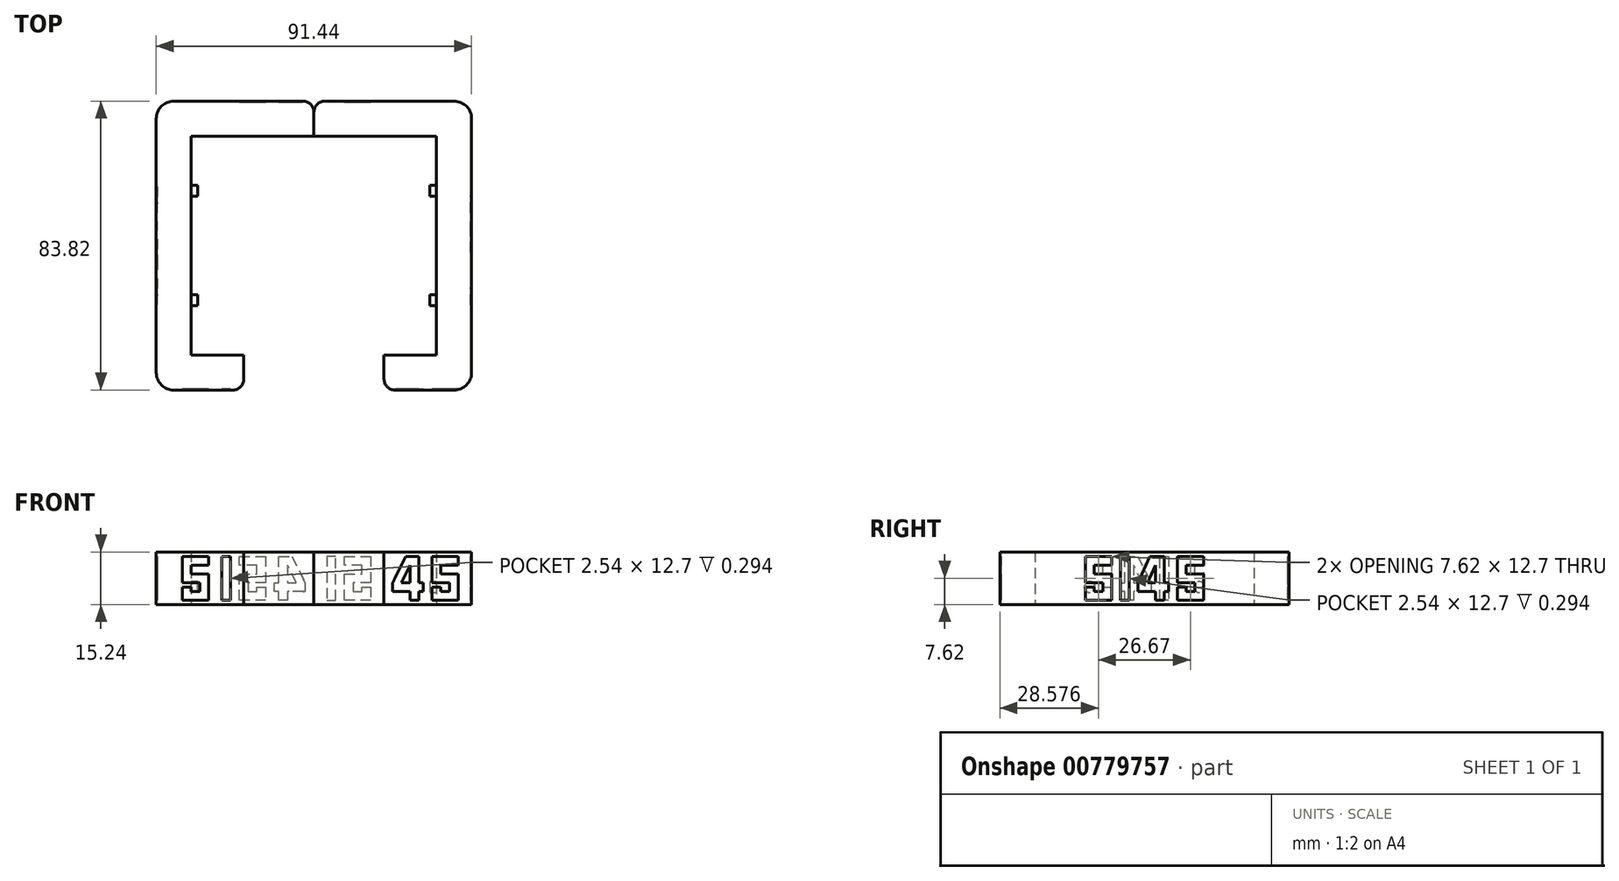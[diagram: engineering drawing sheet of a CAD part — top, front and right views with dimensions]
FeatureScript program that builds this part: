
annotation { "Feature Type Name" : "Feature", "Feature Type Description" : "" }
export const myFeature = defineFeature(function(context is Context, id is Id, definition is map)
    precondition{}
    {
        {
            var Q0;
            Q0=qCreatedBy(makeId("Top.planeOp"),FACE);
            var sketch = newSketch(context, id + "F0", { "sketchPlane" : qUnion([Q0])});
            skLineSegment(sketch, "E0", {"start": v(0, 28.67) * mm, "end": v(0, 38.83) * mm});
            skLineSegment(sketch, "E1", {"start": v(0, 38.83) * mm, "end": v(45.72, 38.83) * mm});
            skLineSegment(sketch, "E2", {"start": v(45.72, 38.83) * mm, "end": v(45.72, -44.99) * mm});
            skLineSegment(sketch, "E3", {"start": v(45.72, -44.99) * mm, "end": v(20.32, -44.99) * mm});
            skLineSegment(sketch, "E4", {"start": v(20.32, -44.99) * mm, "end": v(20.32, -34.83) * mm});
            skLineSegment(sketch, "E5", {"start": v(20.32, -34.83) * mm, "end": v(35.56, -34.83) * mm});
            skLineSegment(sketch, "E6", {"start": v(35.56, -34.83) * mm, "end": v(35.56, 28.67) * mm});
            skLineSegment(sketch, "E7", {"start": v(35.56, 28.67) * mm, "end": v(0, 28.67) * mm});
            skSolve(sketch);
        }
        {
            var Q0;
            Q0=makeQuery(id+"F0.imprint","IMPRINT",FACE,{"disambiguationData":[TD([[makeQuery(id+"F0.imprint","IMPRINT",EDGE,{"derivedFrom":sQuery(id+"F0.wireOp",EDGE,"E0")}),-1.0]])]});
            extrude(context, id + "F1", {"entities" : qUnion([Q0]), "depth" : 15.24 * mm, "offsetDistance" : 25.4 * mm});
        }
        {
            var Q0;
            Q0=makeQuery(id+"F1.opExtrude","SWEPT_FACE",FACE,{"disambiguationData":[OSD([sQuery(id+"F0.wireOp",EDGE,"E6")])]});
            var sketch = newSketch(context, id + "F2", { "sketchPlane" : qUnion([Q0])});
            skCircle(sketch, "E8", {"center": v(-12.8, 5.08) * mm, "radius": 1.59 * mm});
            skPoint(sketch, "E8.centerSnap0", {"position": v(-28.67, 5.08) * mm});
            skCircle(sketch, "E9", {"center": v(18.95, 5.08) * mm, "radius": 1.59 * mm});
            skPoint(sketch, "E9.centerSnap0", {"position": v(34.83, 5.08) * mm});
            skSolve(sketch);
        }
        {
            var Q0;
            Q0=makeQuery(id+"F2.imprint","IMPRINT",FACE,{"disambiguationData":[TD([[makeQuery(id+"F2.imprint","IMPRINT",EDGE,{"derivedFrom":sQuery(id+"F2.wireOp",EDGE,"E8")}),1.0]])]});
            var Q1;
            Q1=makeQuery(id+"F2.imprint","IMPRINT",FACE,{"disambiguationData":[TD([[makeQuery(id+"F2.imprint","IMPRINT",EDGE,{"derivedFrom":sQuery(id+"F2.wireOp",EDGE,"E9")}),1.0]])]});
            extrude(context, id + "F3", {"entities" : qUnion([Q0, Q1]), "operationType" : NewBodyOperationType.ADD, "depth" : 1.9 * mm, "offsetDistance" : 25.4 * mm});
        }
        {
            var Q0;
            Q0=qCreatedBy(makeId("Top.planeOp"),FACE);
            var sketch = newSketch(context, id + "F4", { "sketchPlane" : qUnion([Q0])});
            skLineSegment(sketch, "E10", {"start": v(0, 28.67) * mm, "end": v(-35.56, 28.67) * mm});
            skLineSegment(sketch, "E11", {"start": v(-35.56, 28.67) * mm, "end": v(-35.56, -34.83) * mm});
            skLineSegment(sketch, "E12", {"start": v(-35.56, -34.83) * mm, "end": v(-20.32, -34.83) * mm});
            skLineSegment(sketch, "E13", {"start": v(-20.32, -34.83) * mm, "end": v(-20.32, -44.99) * mm});
            skLineSegment(sketch, "E14", {"start": v(-20.32, -44.99) * mm, "end": v(-45.72, -44.99) * mm});
            skLineSegment(sketch, "E15", {"start": v(-45.72, -44.99) * mm, "end": v(-45.72, 38.83) * mm});
            skLineSegment(sketch, "E16", {"start": v(-45.72, 38.83) * mm, "end": v(0, 38.83) * mm});
            skLineSegment(sketch, "E17", {"start": v(0, 38.83) * mm, "end": v(0, 28.67) * mm});
            skSolve(sketch);
        }
        {
            var Q0;
            Q0=makeQuery(id+"F4.imprint","IMPRINT",FACE,{"disambiguationData":[TD([[makeQuery(id+"F4.imprint","IMPRINT",EDGE,{"derivedFrom":sQuery(id+"F4.wireOp",EDGE,"E10")}),-1.0]])]});
            extrude(context, id + "F5", {"entities" : qUnion([Q0]), "depth" : 15.24 * mm, "offsetDistance" : 25.4 * mm});
        }
        {
            var Q0;
            Q0=makeQuery(id+"F5.opExtrude","SWEPT_FACE",FACE,{"disambiguationData":[OSD([sQuery(id+"F4.wireOp",EDGE,"E11")])]});
            var sketch = newSketch(context, id + "F6", { "sketchPlane" : qUnion([Q0])});
            skCircle(sketch, "E18", {"center": v(-18.95, 5.08) * mm, "radius": 1.59 * mm});
            skPoint(sketch, "E18.centerSnap0", {"position": v(-34.83, 7.62) * mm});
            skCircle(sketch, "E19", {"center": v(12.8, 5.08) * mm, "radius": 1.59 * mm});
            skSolve(sketch);
        }
        {
            var Q0;
            Q0=makeQuery(id+"F6.imprint","IMPRINT",FACE,{"disambiguationData":[TD([[makeQuery(id+"F6.imprint","IMPRINT",EDGE,{"derivedFrom":sQuery(id+"F6.wireOp",EDGE,"E19")}),1.0]])]});
            var Q1;
            Q1=makeQuery(id+"F6.imprint","IMPRINT",FACE,{"disambiguationData":[TD([[makeQuery(id+"F6.imprint","IMPRINT",EDGE,{"derivedFrom":sQuery(id+"F6.wireOp",EDGE,"E18")}),1.0]])]});
            extrude(context, id + "F7", {"entities" : qUnion([Q0, Q1]), "operationType" : NewBodyOperationType.ADD, "depth" : 1.9 * mm, "offsetDistance" : 25.4 * mm});
        }
        {
            var Q0;
            Q0=makeQuery(id+"F1.opExtrude","SWEPT_FACE",FACE,{"disambiguationData":[OSD([sQuery(id+"F0.wireOp",EDGE,"E2")])]});
            var sketch = newSketch(context, id + "F8", { "sketchPlane" : qUnion([Q0])});
            skLineSegment(sketch, "E20", {"start": v(-12.6, 13.97) * mm, "end": v(-20.22, 13.97) * mm});
            skLineSegment(sketch, "E21", {"start": v(-20.22, 13.97) * mm, "end": v(-20.22, 6.35) * mm});
            skLineSegment(sketch, "E22", {"start": v(-20.22, 6.35) * mm, "end": v(-15.14, 6.35) * mm});
            skLineSegment(sketch, "E23", {"start": v(-15.14, 6.35) * mm, "end": v(-15.14, 3.81) * mm});
            skLineSegment(sketch, "E24", {"start": v(-15.14, 3.8) * mm, "end": v(-17.68, 3.8) * mm});
            skLineSegment(sketch, "E25", {"start": v(-17.68, 3.81) * mm, "end": v(-17.68, 5.08) * mm});
            skLineSegment(sketch, "E26", {"start": v(-17.68, 5.08) * mm, "end": v(-20.22, 5.08) * mm});
            skLineSegment(sketch, "E27", {"start": v(-20.22, 5.08) * mm, "end": v(-20.22, 1.27) * mm});
            skLineSegment(sketch, "E28", {"start": v(-20.22, 1.27) * mm, "end": v(-12.6, 1.27) * mm});
            skLineSegment(sketch, "E29", {"start": v(-12.6, 1.27) * mm, "end": v(-12.6, 8.9) * mm});
            skLineSegment(sketch, "E30", {"start": v(-12.6, 8.89) * mm, "end": v(-17.68, 8.89) * mm});
            skLineSegment(sketch, "E31", {"start": v(-17.68, 8.9) * mm, "end": v(-17.68, 11.43) * mm});
            skLineSegment(sketch, "E32", {"start": v(-17.68, 11.43) * mm, "end": v(-12.6, 11.43) * mm});
            skLineSegment(sketch, "E33", {"start": v(-12.6, 11.43) * mm, "end": v(-12.6, 13.97) * mm});
            skLineSegment(sketch, "E34", {"start": v(-10.06, 13.97) * mm, "end": v(-10.06, 1.27) * mm});
            skLineSegment(sketch, "E35", {"start": v(-10.06, 1.27) * mm, "end": v(-7.52, 1.27) * mm});
            skLineSegment(sketch, "E36", {"start": v(-7.52, 1.27) * mm, "end": v(-7.52, 13.97) * mm});
            skLineSegment(sketch, "E37", {"start": v(-7.52, 13.97) * mm, "end": v(-10.06, 13.97) * mm});
            skLineSegment(sketch, "E38", {"start": v(-1.54, 13.97) * mm, "end": v(-4.98, 6.35) * mm});
            skLineSegment(sketch, "E39", {"start": v(-4.98, 6.35) * mm, "end": v(-4.98, 3.81) * mm});
            skLineSegment(sketch, "E40", {"start": v(-4.98, 3.81) * mm, "end": v(0.1, 3.81) * mm});
            skLineSegment(sketch, "E41", {"start": v(0.1, 3.81) * mm, "end": v(0.1, 1.27) * mm});
            skLineSegment(sketch, "E42", {"start": v(0.1, 1.27) * mm, "end": v(2.64, 1.27) * mm});
            skLineSegment(sketch, "E43", {"start": v(2.64, 1.27) * mm, "end": v(2.64, 3.81) * mm});
            skLineSegment(sketch, "E44", {"start": v(2.64, 3.81) * mm, "end": v(3.9, 3.81) * mm});
            skLineSegment(sketch, "E45", {"start": v(3.9, 3.81) * mm, "end": v(3.9, 6.35) * mm});
            skLineSegment(sketch, "E46", {"start": v(3.9, 6.35) * mm, "end": v(2.64, 6.35) * mm});
            skLineSegment(sketch, "E47", {"start": v(2.64, 6.35) * mm, "end": v(2.64, 13.97) * mm});
            skLineSegment(sketch, "E48", {"start": v(2.64, 13.97) * mm, "end": v(-1.54, 13.97) * mm});
            skLineSegment(sketch, "E49", {"start": v(0.1, 6.35) * mm, "end": v(-2.2, 6.35) * mm});
            skLineSegment(sketch, "E50", {"start": v(-2.2, 6.35) * mm, "end": v(0.1, 11.43) * mm});
            skLineSegment(sketch, "E51", {"start": v(0.1, 11.43) * mm, "end": v(0.1, 6.35) * mm});
            skLineSegment(sketch, "E52", {"start": v(14.07, 13.97) * mm, "end": v(6.45, 13.97) * mm});
            skLineSegment(sketch, "E53", {"start": v(6.45, 13.97) * mm, "end": v(6.45, 6.35) * mm});
            skLineSegment(sketch, "E54", {"start": v(6.45, 6.35) * mm, "end": v(11.53, 6.35) * mm});
            skLineSegment(sketch, "E55", {"start": v(11.53, 6.35) * mm, "end": v(11.53, 3.81) * mm});
            skLineSegment(sketch, "E56", {"start": v(11.53, 3.81) * mm, "end": v(8.99, 3.81) * mm});
            skPoint(sketch, "E56.endSnap0", {"position": v(8.99, 6.35) * mm});
            skLineSegment(sketch, "E57", {"start": v(8.99, 3.81) * mm, "end": v(8.99, 5.08) * mm});
            skPoint(sketch, "E57.endSnap0", {"position": v(11.53, 5.08) * mm});
            skLineSegment(sketch, "E58", {"start": v(8.99, 5.08) * mm, "end": v(6.45, 5.08) * mm});
            skLineSegment(sketch, "E59", {"start": v(6.45, 5.08) * mm, "end": v(6.45, 1.27) * mm});
            skLineSegment(sketch, "E60", {"start": v(6.45, 1.27) * mm, "end": v(14.07, 1.27) * mm});
            skLineSegment(sketch, "E61", {"start": v(14.07, 1.27) * mm, "end": v(14.07, 8.9) * mm});
            skLineSegment(sketch, "E62", {"start": v(14.07, 8.9) * mm, "end": v(8.99, 8.9) * mm});
            skLineSegment(sketch, "E63", {"start": v(8.99, 8.9) * mm, "end": v(8.99, 11.43) * mm});
            skLineSegment(sketch, "E64", {"start": v(8.99, 11.43) * mm, "end": v(14.07, 11.43) * mm});
            skLineSegment(sketch, "E65", {"start": v(14.07, 11.43) * mm, "end": v(14.07, 13.97) * mm});
            skLineSegment(sketch, "E66", {"start": v(-20.22, 13.97) * mm, "end": v(-44.99, 13.97) * mm});
            skLineSegment(sketch, "E67", {"start": v(14.07, 13.97) * mm, "end": v(38.83, 13.97) * mm});
            skSolve(sketch);
        }
        {
            var Q0;
            Q0=makeQuery(id+"F8.imprint","IMPRINT",FACE,{"disambiguationData":[TD([[makeQuery(id+"F8.imprint","IMPRINT",EDGE,{"derivedFrom":sQuery(id+"F8.wireOp",EDGE,"E20")}),1.0]])]});
            var Q1;
            Q1=makeQuery(id+"F8.imprint","IMPRINT",FACE,{"disambiguationData":[TD([[makeQuery(id+"F8.imprint","IMPRINT",EDGE,{"derivedFrom":sQuery(id+"F8.wireOp",EDGE,"E34")}),1.0]])]});
            var Q2;
            Q2=makeQuery(id+"F8.imprint","IMPRINT",FACE,{"disambiguationData":[TD([[makeQuery(id+"F8.imprint","IMPRINT",EDGE,{"derivedFrom":sQuery(id+"F8.wireOp",EDGE,"E38")}),1.0]])]});
            var Q3;
            Q3=makeQuery(id+"F8.imprint","IMPRINT",FACE,{"disambiguationData":[TD([[makeQuery(id+"F8.imprint","IMPRINT",EDGE,{"derivedFrom":sQuery(id+"F8.wireOp",EDGE,"E52")}),1.0]])]});
            extrude(context, id + "F9", {"entities" : qUnion([Q0, Q1, Q2, Q3]), "operationType" : NewBodyOperationType.REMOVE, "oppositeDirection" : true, "depth" : 0.8 * mm, "offsetDistance" : 25.4 * mm});
        }
        {
            var Q0;
            Q0=makeQuery(id+"F1.opExtrude","SWEPT_FACE",FACE,{"disambiguationData":[OSD([sQuery(id+"F0.wireOp",EDGE,"E3")])]});
            var sketch = newSketch(context, id + "F10", { "sketchPlane" : qUnion([Q0])});
            skLineSegment(sketch, "E68", {"start": v(22.86, 6.35) * mm, "end": v(22.86, 3.81) * mm});
            skLineSegment(sketch, "E69", {"start": v(22.86, 3.81) * mm, "end": v(27.94, 3.81) * mm});
            skLineSegment(sketch, "E70", {"start": v(27.94, 3.81) * mm, "end": v(27.94, 1.27) * mm});
            skLineSegment(sketch, "E71", {"start": v(27.94, 1.27) * mm, "end": v(30.48, 1.27) * mm});
            skLineSegment(sketch, "E72", {"start": v(30.48, 1.27) * mm, "end": v(30.48, 3.81) * mm});
            skLineSegment(sketch, "E73", {"start": v(30.48, 3.81) * mm, "end": v(31.75, 3.81) * mm});
            skLineSegment(sketch, "E74", {"start": v(31.75, 3.81) * mm, "end": v(31.75, 6.35) * mm});
            skLineSegment(sketch, "E75", {"start": v(31.75, 6.35) * mm, "end": v(30.48, 6.35) * mm});
            skLineSegment(sketch, "E76", {"start": v(30.48, 6.35) * mm, "end": v(30.48, 13.97) * mm});
            skLineSegment(sketch, "E77", {"start": v(30.48, 13.97) * mm, "end": v(26.67, 13.97) * mm});
            skLineSegment(sketch, "E78", {"start": v(26.67, 13.97) * mm, "end": v(22.86, 6.35) * mm});
            skLineSegment(sketch, "E79", {"start": v(27.94, 6.35) * mm, "end": v(25.4, 6.35) * mm});
            skLineSegment(sketch, "E80", {"start": v(25.4, 6.35) * mm, "end": v(27.94, 11.43) * mm});
            skLineSegment(sketch, "E81", {"start": v(27.94, 11.43) * mm, "end": v(27.94, 6.35) * mm});
            skLineSegment(sketch, "E82", {"start": v(41.91, 13.97) * mm, "end": v(34.3, 13.97) * mm});
            skLineSegment(sketch, "E83", {"start": v(34.3, 13.97) * mm, "end": v(34.3, 6.35) * mm});
            skLineSegment(sketch, "E84", {"start": v(34.3, 6.35) * mm, "end": v(39.37, 6.35) * mm});
            skLineSegment(sketch, "E85", {"start": v(39.37, 6.35) * mm, "end": v(39.37, 3.81) * mm});
            skLineSegment(sketch, "E86", {"start": v(39.37, 3.81) * mm, "end": v(36.83, 3.81) * mm});
            skPoint(sketch, "E86.endSnap0", {"position": v(36.83, 6.35) * mm});
            skLineSegment(sketch, "E87", {"start": v(36.83, 3.81) * mm, "end": v(36.83, 5.08) * mm});
            skPoint(sketch, "E87.endSnap0", {"position": v(39.37, 5.08) * mm});
            skLineSegment(sketch, "E88", {"start": v(36.83, 5.08) * mm, "end": v(34.3, 5.08) * mm});
            skLineSegment(sketch, "E89", {"start": v(34.3, 5.08) * mm, "end": v(34.3, 1.27) * mm});
            skLineSegment(sketch, "E90", {"start": v(34.3, 1.27) * mm, "end": v(41.91, 1.27) * mm});
            skLineSegment(sketch, "E91", {"start": v(41.91, 1.27) * mm, "end": v(41.91, 8.89) * mm});
            skLineSegment(sketch, "E92", {"start": v(41.91, 8.89) * mm, "end": v(36.83, 8.89) * mm});
            skLineSegment(sketch, "E93", {"start": v(36.83, 8.89) * mm, "end": v(36.83, 11.43) * mm});
            skLineSegment(sketch, "E94", {"start": v(36.83, 11.43) * mm, "end": v(41.91, 11.43) * mm});
            skLineSegment(sketch, "E95", {"start": v(41.91, 11.43) * mm, "end": v(41.91, 13.97) * mm});
            skSolve(sketch);
        }
        {
            var Q0;
            Q0=makeQuery(id+"F10.imprint","IMPRINT",FACE,{"disambiguationData":[TD([[makeQuery(id+"F10.imprint","IMPRINT",EDGE,{"derivedFrom":sQuery(id+"F10.wireOp",EDGE,"E68")}),1.0]])]});
            var Q1;
            Q1=makeQuery(id+"F10.imprint","IMPRINT",FACE,{"disambiguationData":[TD([[makeQuery(id+"F10.imprint","IMPRINT",EDGE,{"derivedFrom":sQuery(id+"F10.wireOp",EDGE,"E82")}),1.0]])]});
            extrude(context, id + "F11", {"entities" : qUnion([Q0, Q1]), "operationType" : NewBodyOperationType.REMOVE, "oppositeDirection" : true, "depth" : 0.8 * mm, "offsetDistance" : 25.4 * mm});
        }
        {
            var Q0;
            Q0=makeQuery(id+"F5.opExtrude","SWEPT_FACE",FACE,{"disambiguationData":[OSD([sQuery(id+"F4.wireOp",EDGE,"E14")])]});
            var sketch = newSketch(context, id + "F12", { "sketchPlane" : qUnion([Q0])});
            skLineSegment(sketch, "E96", {"start": v(-24.13, 13.97) * mm, "end": v(-26.67, 13.97) * mm});
            skLineSegment(sketch, "E97", {"start": v(-26.67, 13.97) * mm, "end": v(-26.67, 1.27) * mm});
            skLineSegment(sketch, "E98", {"start": v(-26.67, 1.27) * mm, "end": v(-24.13, 1.27) * mm});
            skLineSegment(sketch, "E99", {"start": v(-24.13, 1.27) * mm, "end": v(-24.13, 13.97) * mm});
            skLineSegment(sketch, "E100", {"start": v(-30.48, 13.97) * mm, "end": v(-38.1, 13.97) * mm});
            skLineSegment(sketch, "E101", {"start": v(-38.1, 13.97) * mm, "end": v(-38.1, 6.35) * mm});
            skLineSegment(sketch, "E102", {"start": v(-38.1, 6.35) * mm, "end": v(-33.02, 6.35) * mm});
            skLineSegment(sketch, "E103", {"start": v(-33.02, 6.35) * mm, "end": v(-33.02, 3.8) * mm});
            skLineSegment(sketch, "E104", {"start": v(-33.02, 3.8) * mm, "end": v(-35.56, 3.8) * mm});
            skLineSegment(sketch, "E105", {"start": v(-35.56, 3.8) * mm, "end": v(-35.56, 5.08) * mm});
            skLineSegment(sketch, "E106", {"start": v(-35.56, 5.08) * mm, "end": v(-38.1, 5.08) * mm});
            skLineSegment(sketch, "E107", {"start": v(-38.1, 5.08) * mm, "end": v(-38.1, 1.27) * mm});
            skLineSegment(sketch, "E108", {"start": v(-38.1, 1.27) * mm, "end": v(-30.48, 1.27) * mm});
            skLineSegment(sketch, "E109", {"start": v(-30.48, 1.27) * mm, "end": v(-30.48, 8.9) * mm});
            skLineSegment(sketch, "E110", {"start": v(-30.48, 8.89) * mm, "end": v(-35.56, 8.89) * mm});
            skLineSegment(sketch, "E111", {"start": v(-35.56, 8.89) * mm, "end": v(-35.56, 11.43) * mm});
            skLineSegment(sketch, "E112", {"start": v(-35.56, 11.43) * mm, "end": v(-30.48, 11.43) * mm});
            skLineSegment(sketch, "E113", {"start": v(-30.48, 11.43) * mm, "end": v(-30.48, 13.97) * mm});
            skSolve(sketch);
        }
        {
            var Q0;
            Q0=makeQuery(id+"F12.imprint","IMPRINT",FACE,{"disambiguationData":[TD([[makeQuery(id+"F12.imprint","IMPRINT",EDGE,{"derivedFrom":sQuery(id+"F12.wireOp",EDGE,"E100")}),1.0]])]});
            var Q1;
            Q1=makeQuery(id+"F12.imprint","IMPRINT",FACE,{"disambiguationData":[TD([[makeQuery(id+"F12.imprint","IMPRINT",EDGE,{"derivedFrom":sQuery(id+"F12.wireOp",EDGE,"E96")}),1.0]])]});
            extrude(context, id + "F13", {"entities" : qUnion([Q0, Q1]), "operationType" : NewBodyOperationType.REMOVE, "oppositeDirection" : true, "depth" : 0.8 * mm, "offsetDistance" : 25.4 * mm});
        }
        {
            var Q0;
            Q0=makeQuery(id+"F5.opExtrude","SWEPT_FACE",FACE,{"disambiguationData":[OSD([sQuery(id+"F4.wireOp",EDGE,"E15")])]});
            var sketch = newSketch(context, id + "F14", { "sketchPlane" : qUnion([Q0])});
            skLineSegment(sketch, "E114", {"start": v(-6.45, 13.97) * mm, "end": v(-14.07, 13.97) * mm});
            skLineSegment(sketch, "E115", {"start": v(-14.07, 13.97) * mm, "end": v(-14.07, 6.35) * mm});
            skLineSegment(sketch, "E116", {"start": v(-14.07, 6.35) * mm, "end": v(-8.99, 6.35) * mm});
            skLineSegment(sketch, "E117", {"start": v(-8.99, 6.35) * mm, "end": v(-8.99, 3.8) * mm});
            skLineSegment(sketch, "E118", {"start": v(-8.99, 3.81) * mm, "end": v(-11.53, 3.81) * mm});
            skLineSegment(sketch, "E119", {"start": v(-11.53, 3.8) * mm, "end": v(-11.53, 5.08) * mm});
            skLineSegment(sketch, "E120", {"start": v(-11.53, 5.08) * mm, "end": v(-14.07, 5.08) * mm});
            skLineSegment(sketch, "E121", {"start": v(-14.07, 5.08) * mm, "end": v(-14.07, 1.27) * mm});
            skLineSegment(sketch, "E122", {"start": v(-14.07, 1.27) * mm, "end": v(-6.45, 1.27) * mm});
            skLineSegment(sketch, "E123", {"start": v(-6.45, 1.27) * mm, "end": v(-6.45, 8.9) * mm});
            skLineSegment(sketch, "E124", {"start": v(-6.45, 8.9) * mm, "end": v(-11.53, 8.9) * mm});
            skLineSegment(sketch, "E125", {"start": v(-11.53, 8.89) * mm, "end": v(-11.53, 11.43) * mm});
            skLineSegment(sketch, "E126", {"start": v(-11.53, 11.43) * mm, "end": v(-6.45, 11.43) * mm});
            skLineSegment(sketch, "E127", {"start": v(-6.45, 11.43) * mm, "end": v(-6.45, 13.97) * mm});
            skLineSegment(sketch, "E128", {"start": v(-3.9, 13.97) * mm, "end": v(-3.9, 1.27) * mm});
            skLineSegment(sketch, "E129", {"start": v(-3.9, 1.27) * mm, "end": v(-1.37, 1.27) * mm});
            skLineSegment(sketch, "E130", {"start": v(-1.37, 1.27) * mm, "end": v(-1.37, 13.97) * mm});
            skLineSegment(sketch, "E131", {"start": v(-1.37, 13.97) * mm, "end": v(-3.9, 13.97) * mm});
            skLineSegment(sketch, "E132", {"start": v(4.98, 13.97) * mm, "end": v(1.17, 6.35) * mm});
            skLineSegment(sketch, "E133", {"start": v(1.17, 6.35) * mm, "end": v(1.17, 3.81) * mm});
            skLineSegment(sketch, "E134", {"start": v(1.17, 3.81) * mm, "end": v(6.25, 3.81) * mm});
            skLineSegment(sketch, "E135", {"start": v(6.25, 3.81) * mm, "end": v(6.25, 1.27) * mm});
            skLineSegment(sketch, "E136", {"start": v(6.25, 1.27) * mm, "end": v(8.8, 1.27) * mm});
            skLineSegment(sketch, "E137", {"start": v(8.8, 1.27) * mm, "end": v(8.8, 3.81) * mm});
            skLineSegment(sketch, "E138", {"start": v(8.8, 3.81) * mm, "end": v(10.06, 3.81) * mm});
            skLineSegment(sketch, "E139", {"start": v(10.06, 3.81) * mm, "end": v(10.06, 6.35) * mm});
            skLineSegment(sketch, "E140", {"start": v(10.06, 6.35) * mm, "end": v(8.8, 6.35) * mm});
            skLineSegment(sketch, "E141", {"start": v(8.8, 6.35) * mm, "end": v(8.8, 13.97) * mm});
            skLineSegment(sketch, "E142", {"start": v(8.8, 13.97) * mm, "end": v(4.98, 13.97) * mm});
            skLineSegment(sketch, "E143", {"start": v(6.25, 6.35) * mm, "end": v(3.71, 6.35) * mm});
            skLineSegment(sketch, "E144", {"start": v(3.71, 6.35) * mm, "end": v(6.25, 11.43) * mm});
            skLineSegment(sketch, "E145", {"start": v(6.25, 11.43) * mm, "end": v(6.25, 6.35) * mm});
            skLineSegment(sketch, "E146", {"start": v(20.22, 13.97) * mm, "end": v(12.6, 13.97) * mm});
            skLineSegment(sketch, "E147", {"start": v(12.6, 13.97) * mm, "end": v(12.6, 6.35) * mm});
            skLineSegment(sketch, "E148", {"start": v(12.6, 6.35) * mm, "end": v(17.68, 6.35) * mm});
            skLineSegment(sketch, "E149", {"start": v(17.68, 6.35) * mm, "end": v(17.68, 3.81) * mm});
            skLineSegment(sketch, "E150", {"start": v(17.68, 3.81) * mm, "end": v(15.14, 3.81) * mm});
            skLineSegment(sketch, "E151", {"start": v(15.14, 3.81) * mm, "end": v(15.14, 5.08) * mm});
            skLineSegment(sketch, "E152", {"start": v(15.14, 5.08) * mm, "end": v(12.6, 5.08) * mm});
            skLineSegment(sketch, "E153", {"start": v(12.6, 5.08) * mm, "end": v(12.6, 1.27) * mm});
            skLineSegment(sketch, "E154", {"start": v(12.6, 1.27) * mm, "end": v(20.22, 1.27) * mm});
            skLineSegment(sketch, "E155", {"start": v(20.22, 1.27) * mm, "end": v(20.22, 8.9) * mm});
            skLineSegment(sketch, "E156", {"start": v(20.22, 8.9) * mm, "end": v(15.14, 8.9) * mm});
            skLineSegment(sketch, "E157", {"start": v(15.14, 8.9) * mm, "end": v(15.14, 11.43) * mm});
            skLineSegment(sketch, "E158", {"start": v(15.14, 11.43) * mm, "end": v(20.22, 11.43) * mm});
            skLineSegment(sketch, "E159", {"start": v(20.22, 11.43) * mm, "end": v(20.22, 13.97) * mm});
            skLineSegment(sketch, "E160", {"start": v(-38.83, 13.97) * mm, "end": v(-14.07, 13.97) * mm});
            skLineSegment(sketch, "E161", {"start": v(44.99, 13.97) * mm, "end": v(20.22, 13.97) * mm});
            skSolve(sketch);
        }
        {
            var Q0;
            Q0 = qSketchRegion(id + "F14", true);
            extrude(context, id + "F15", {"entities" : qUnion([Q0]), "operationType" : NewBodyOperationType.REMOVE, "oppositeDirection" : true, "depth" : 0.8 * mm, "offsetDistance" : 25.4 * mm});
        }
        {
            var Q0;
            Q0=makeQuery(id+"F1.opExtrude","SWEPT_FACE",FACE,{"disambiguationData":[OSD([sQuery(id+"F0.wireOp",EDGE,"E1")])]});
            var sketch = newSketch(context, id + "F16", { "sketchPlane" : qUnion([Q0])});
            skLineSegment(sketch, "E162", {"start": v(-8.9, 13.97) * mm, "end": v(-16.51, 13.97) * mm});
            skLineSegment(sketch, "E163", {"start": v(-16.51, 13.97) * mm, "end": v(-16.51, 6.35) * mm});
            skLineSegment(sketch, "E164", {"start": v(-16.51, 6.35) * mm, "end": v(-11.43, 6.35) * mm});
            skLineSegment(sketch, "E165", {"start": v(-11.43, 6.35) * mm, "end": v(-11.43, 3.81) * mm});
            skLineSegment(sketch, "E166", {"start": v(-11.43, 3.81) * mm, "end": v(-13.97, 3.8) * mm});
            skLineSegment(sketch, "E167", {"start": v(-13.97, 3.8) * mm, "end": v(-13.97, 5.08) * mm});
            skLineSegment(sketch, "E168", {"start": v(-13.97, 5.08) * mm, "end": v(-16.51, 5.08) * mm});
            skLineSegment(sketch, "E169", {"start": v(-16.51, 5.08) * mm, "end": v(-16.51, 1.27) * mm});
            skLineSegment(sketch, "E170", {"start": v(-16.51, 1.27) * mm, "end": v(-8.9, 1.27) * mm});
            skLineSegment(sketch, "E171", {"start": v(-8.9, 1.27) * mm, "end": v(-8.9, 8.89) * mm});
            skLineSegment(sketch, "E172", {"start": v(-8.9, 8.9) * mm, "end": v(-13.97, 8.89) * mm});
            skLineSegment(sketch, "E173", {"start": v(-13.97, 8.89) * mm, "end": v(-13.97, 11.43) * mm});
            skLineSegment(sketch, "E174", {"start": v(-13.97, 11.43) * mm, "end": v(-8.9, 11.43) * mm});
            skLineSegment(sketch, "E175", {"start": v(-8.9, 11.43) * mm, "end": v(-8.9, 13.97) * mm});
            skLineSegment(sketch, "E176", {"start": v(-6.35, 13.97) * mm, "end": v(-3.81, 13.97) * mm});
            skLineSegment(sketch, "E177", {"start": v(-3.81, 13.97) * mm, "end": v(-3.81, 1.27) * mm});
            skLineSegment(sketch, "E178", {"start": v(-3.81, 1.27) * mm, "end": v(-6.35, 1.27) * mm});
            skLineSegment(sketch, "E179", {"start": v(-6.35, 1.27) * mm, "end": v(-6.35, 13.97) * mm});
            skSolve(sketch);
        }
        {
            var Q0;
            Q0 = qSketchRegion(id + "F16", true);
            extrude(context, id + "F17", {"entities" : qUnion([Q0]), "operationType" : NewBodyOperationType.REMOVE, "oppositeDirection" : true, "depth" : 0.8 * mm, "offsetDistance" : 25.4 * mm});
        }
        {
            var Q0;
            Q0=makeQuery(id+"F5.opExtrude","SWEPT_FACE",FACE,{"disambiguationData":[OSD([sQuery(id+"F4.wireOp",EDGE,"E16")])]});
            var sketch = newSketch(context, id + "F18", { "sketchPlane" : qUnion([Q0])});
            skLineSegment(sketch, "E180", {"start": v(2.54, 6.35) * mm, "end": v(2.54, 3.81) * mm});
            skLineSegment(sketch, "E181", {"start": v(2.54, 3.81) * mm, "end": v(7.62, 3.81) * mm});
            skLineSegment(sketch, "E182", {"start": v(7.62, 3.81) * mm, "end": v(7.62, 1.27) * mm});
            skLineSegment(sketch, "E183", {"start": v(7.62, 1.27) * mm, "end": v(10.16, 1.27) * mm});
            skLineSegment(sketch, "E184", {"start": v(10.16, 1.27) * mm, "end": v(10.16, 3.81) * mm});
            skLineSegment(sketch, "E185", {"start": v(10.16, 3.81) * mm, "end": v(11.43, 3.81) * mm});
            skLineSegment(sketch, "E186", {"start": v(11.43, 3.81) * mm, "end": v(11.43, 6.35) * mm});
            skLineSegment(sketch, "E187", {"start": v(11.43, 6.35) * mm, "end": v(10.16, 6.35) * mm});
            skLineSegment(sketch, "E188", {"start": v(10.16, 6.35) * mm, "end": v(10.16, 13.97) * mm});
            skLineSegment(sketch, "E189", {"start": v(10.16, 13.97) * mm, "end": v(6.35, 13.97) * mm});
            skLineSegment(sketch, "E190", {"start": v(6.35, 13.97) * mm, "end": v(2.54, 6.35) * mm});
            skLineSegment(sketch, "E191", {"start": v(7.62, 6.35) * mm, "end": v(5.08, 6.35) * mm});
            skLineSegment(sketch, "E192", {"start": v(5.08, 6.35) * mm, "end": v(7.62, 11.43) * mm});
            skLineSegment(sketch, "E193", {"start": v(7.62, 11.43) * mm, "end": v(7.62, 6.35) * mm});
            skLineSegment(sketch, "E194", {"start": v(21.6, 13.97) * mm, "end": v(13.97, 13.97) * mm});
            skLineSegment(sketch, "E195", {"start": v(13.97, 13.97) * mm, "end": v(13.97, 6.35) * mm});
            skLineSegment(sketch, "E196", {"start": v(13.97, 6.35) * mm, "end": v(19.05, 6.35) * mm});
            skLineSegment(sketch, "E197", {"start": v(19.05, 6.35) * mm, "end": v(19.05, 3.81) * mm});
            skLineSegment(sketch, "E198", {"start": v(19.05, 3.81) * mm, "end": v(16.51, 3.81) * mm});
            skLineSegment(sketch, "E199", {"start": v(16.51, 3.81) * mm, "end": v(16.51, 5.08) * mm});
            skLineSegment(sketch, "E200", {"start": v(16.51, 5.08) * mm, "end": v(13.97, 5.08) * mm});
            skLineSegment(sketch, "E201", {"start": v(13.97, 5.08) * mm, "end": v(13.97, 1.27) * mm});
            skLineSegment(sketch, "E202", {"start": v(13.97, 1.27) * mm, "end": v(21.59, 1.27) * mm});
            skLineSegment(sketch, "E203", {"start": v(21.59, 1.27) * mm, "end": v(21.59, 8.9) * mm});
            skLineSegment(sketch, "E204", {"start": v(21.59, 8.9) * mm, "end": v(16.51, 8.9) * mm});
            skLineSegment(sketch, "E205", {"start": v(16.51, 8.9) * mm, "end": v(16.51, 11.43) * mm});
            skLineSegment(sketch, "E206", {"start": v(16.51, 11.43) * mm, "end": v(21.59, 11.43) * mm});
            skLineSegment(sketch, "E207", {"start": v(21.59, 11.43) * mm, "end": v(21.59, 13.97) * mm});
            skSolve(sketch);
        }
        {
            var Q0;
            Q0 = qSketchRegion(id + "F18", true);
            extrude(context, id + "F19", {"entities" : qUnion([Q0]), "operationType" : NewBodyOperationType.REMOVE, "oppositeDirection" : true, "depth" : 0.8 * mm, "offsetDistance" : 25.4 * mm});
        }
        {
            var Q0;
            Q0=makeQuery(id+"F5.opExtrude","SWEPT_EDGE",EDGE,{"disambiguationData":[OSD([sQuery(id+"F4.wireOp",EDGE,"E15"),sQuery(id+"F4.wireOp",EDGE,"E16")])]});
            var Q1;
            Q1=makeQuery(id+"F5.opExtrude","SWEPT_EDGE",EDGE,{"disambiguationData":[OSD([sQuery(id+"F4.wireOp",EDGE,"E14"),sQuery(id+"F4.wireOp",EDGE,"E15")])]});
            fillet(context, id + "F20", {"entities" : qUnion([Q0, Q1]), "tangentPropagation" : true, "radius" : 5.08 * mm, "defaultsChanged" : true, "vertexSettings" : [], "allowEdgeOverflow" : false});
        }
        {
            var Q0;
            Q0=makeQuery(id+"F1.opExtrude","SWEPT_EDGE",EDGE,{"disambiguationData":[OSD([sQuery(id+"F0.wireOp",EDGE,"E2"),sQuery(id+"F0.wireOp",EDGE,"E3")])]});
            var Q1;
            Q1=makeQuery(id+"F1.opExtrude","SWEPT_EDGE",EDGE,{"disambiguationData":[OSD([sQuery(id+"F0.wireOp",EDGE,"E1"),sQuery(id+"F0.wireOp",EDGE,"E2")])]});
            fillet(context, id + "F21", {"entities" : qUnion([Q0, Q1]), "tangentPropagation" : true, "radius" : 5.08 * mm, "defaultsChanged" : false, "vertexSettings" : [], "allowEdgeOverflow" : false});
        }
        {
            var Q0;
            Q0=makeQuery(id+"F1.opExtrude","SWEPT_EDGE",EDGE,{"disambiguationData":[OSD([sQuery(id+"F0.wireOp",EDGE,"E3"),sQuery(id+"F0.wireOp",EDGE,"E4")])]});
            var Q1;
            Q1=makeQuery(id+"F5.opExtrude","SWEPT_EDGE",EDGE,{"disambiguationData":[OSD([sQuery(id+"F4.wireOp",EDGE,"E13"),sQuery(id+"F4.wireOp",EDGE,"E14")])]});
            var Q2;
            Q2=makeQuery(id+"F1.opExtrude","SWEPT_EDGE",EDGE,{"disambiguationData":[OSD([sQuery(id+"F0.wireOp",EDGE,"E0"),sQuery(id+"F0.wireOp",EDGE,"E1")])]});
            var Q3;
            Q3=makeQuery(id+"F5.opExtrude","SWEPT_EDGE",EDGE,{"disambiguationData":[OSD([sQuery(id+"F4.wireOp",EDGE,"E16"),sQuery(id+"F4.wireOp",EDGE,"E17")])]});
            fillet(context, id + "F22", {"entities" : qUnion([Q0, Q1, Q2, Q3]), "tangentPropagation" : true, "radius" : 3.17 * mm, "defaultsChanged" : true, "vertexSettings" : [], "allowEdgeOverflow" : false});
        }
        {
            var Q0;
            Q0=makeQuery(id+"F15.boolean.opBoolean","COPY",FACE,{"derivedFrom":makeQuery(id+"F15.opExtrude","CAP_FACE",FACE,{"disambiguationData":[OSD([sQuery(id+"F14.wireOp",EDGE,"E114"),sQuery(id+"F14.wireOp",EDGE,"E115"),sQuery(id+"F14.wireOp",EDGE,"E116"),sQuery(id+"F14.wireOp",EDGE,"E117"),sQuery(id+"F14.wireOp",EDGE,"E118"),sQuery(id+"F14.wireOp",EDGE,"E119"),sQuery(id+"F14.wireOp",EDGE,"E120"),sQuery(id+"F14.wireOp",EDGE,"E121"),sQuery(id+"F14.wireOp",EDGE,"E122"),sQuery(id+"F14.wireOp",EDGE,"E123"),sQuery(id+"F14.wireOp",EDGE,"E124"),sQuery(id+"F14.wireOp",EDGE,"E125"),sQuery(id+"F14.wireOp",EDGE,"E126"),sQuery(id+"F14.wireOp",EDGE,"E127")])],"isStart":false})});
            var Q1;
            Q1=makeQuery(id+"F15.boolean.opBoolean","COPY",FACE,{"derivedFrom":makeQuery(id+"F15.opExtrude","CAP_FACE",FACE,{"disambiguationData":[OSD([sQuery(id+"F14.wireOp",EDGE,"E128"),sQuery(id+"F14.wireOp",EDGE,"E129"),sQuery(id+"F14.wireOp",EDGE,"E130"),sQuery(id+"F14.wireOp",EDGE,"E131")])],"isStart":false})});
            var Q2;
            Q2=makeQuery(id+"F15.boolean.opBoolean","COPY",FACE,{"derivedFrom":makeQuery(id+"F15.opExtrude","CAP_FACE",FACE,{"disambiguationData":[OSD([sQuery(id+"F14.wireOp",EDGE,"E132"),sQuery(id+"F14.wireOp",EDGE,"E133"),sQuery(id+"F14.wireOp",EDGE,"E134"),sQuery(id+"F14.wireOp",EDGE,"E135"),sQuery(id+"F14.wireOp",EDGE,"E136"),sQuery(id+"F14.wireOp",EDGE,"E137"),sQuery(id+"F14.wireOp",EDGE,"E138"),sQuery(id+"F14.wireOp",EDGE,"E139"),sQuery(id+"F14.wireOp",EDGE,"E140"),sQuery(id+"F14.wireOp",EDGE,"E141"),sQuery(id+"F14.wireOp",EDGE,"E142"),sQuery(id+"F14.wireOp",EDGE,"E143"),sQuery(id+"F14.wireOp",EDGE,"E144"),sQuery(id+"F14.wireOp",EDGE,"E145")])],"isStart":false})});
            var Q3;
            Q3=makeQuery(id+"F15.boolean.opBoolean","COPY",FACE,{"derivedFrom":makeQuery(id+"F15.opExtrude","CAP_FACE",FACE,{"disambiguationData":[OSD([sQuery(id+"F14.wireOp",EDGE,"E146"),sQuery(id+"F14.wireOp",EDGE,"E147"),sQuery(id+"F14.wireOp",EDGE,"E148"),sQuery(id+"F14.wireOp",EDGE,"E149"),sQuery(id+"F14.wireOp",EDGE,"E150"),sQuery(id+"F14.wireOp",EDGE,"E151"),sQuery(id+"F14.wireOp",EDGE,"E152"),sQuery(id+"F14.wireOp",EDGE,"E153"),sQuery(id+"F14.wireOp",EDGE,"E154"),sQuery(id+"F14.wireOp",EDGE,"E155"),sQuery(id+"F14.wireOp",EDGE,"E156"),sQuery(id+"F14.wireOp",EDGE,"E157"),sQuery(id+"F14.wireOp",EDGE,"E158"),sQuery(id+"F14.wireOp",EDGE,"E159")])],"isStart":false})});
            extrude(context, id + "F23", {"entities" : qUnion([Q0, Q1, Q2, Q3]), "operationType" : NewBodyOperationType.ADD, "depth" : 0.5 * mm, "offsetDistance" : 25 * mm});
        }
        {
            var Q0;
            Q0=makeQuery(id+"F13.boolean.opBoolean","COPY",FACE,{"derivedFrom":makeQuery(id+"F13.opExtrude","CAP_FACE",FACE,{"disambiguationData":[OSD([sQuery(id+"F12.wireOp",EDGE,"E100"),sQuery(id+"F12.wireOp",EDGE,"E101"),sQuery(id+"F12.wireOp",EDGE,"E102"),sQuery(id+"F12.wireOp",EDGE,"E103"),sQuery(id+"F12.wireOp",EDGE,"E104"),sQuery(id+"F12.wireOp",EDGE,"E105"),sQuery(id+"F12.wireOp",EDGE,"E106"),sQuery(id+"F12.wireOp",EDGE,"E107"),sQuery(id+"F12.wireOp",EDGE,"E108"),sQuery(id+"F12.wireOp",EDGE,"E109"),sQuery(id+"F12.wireOp",EDGE,"E110"),sQuery(id+"F12.wireOp",EDGE,"E111"),sQuery(id+"F12.wireOp",EDGE,"E112"),sQuery(id+"F12.wireOp",EDGE,"E113")])],"isStart":false})});
            var Q1;
            Q1=makeQuery(id+"F13.boolean.opBoolean","COPY",FACE,{"derivedFrom":makeQuery(id+"F13.opExtrude","CAP_FACE",FACE,{"disambiguationData":[OSD([sQuery(id+"F12.wireOp",EDGE,"E96"),sQuery(id+"F12.wireOp",EDGE,"E97"),sQuery(id+"F12.wireOp",EDGE,"E98"),sQuery(id+"F12.wireOp",EDGE,"E99")])],"isStart":false})});
            extrude(context, id + "F24", {"entities" : qUnion([Q0, Q1]), "operationType" : NewBodyOperationType.ADD, "depth" : 0.5 * mm, "offsetDistance" : 25 * mm});
        }
        {
            var Q0;
            Q0=makeQuery(id+"F11.boolean.opBoolean","COPY",FACE,{"derivedFrom":makeQuery(id+"F11.opExtrude","CAP_FACE",FACE,{"disambiguationData":[OSD([sQuery(id+"F10.wireOp",EDGE,"E68"),sQuery(id+"F10.wireOp",EDGE,"E69"),sQuery(id+"F10.wireOp",EDGE,"E70"),sQuery(id+"F10.wireOp",EDGE,"E71"),sQuery(id+"F10.wireOp",EDGE,"E72"),sQuery(id+"F10.wireOp",EDGE,"E73"),sQuery(id+"F10.wireOp",EDGE,"E74"),sQuery(id+"F10.wireOp",EDGE,"E75"),sQuery(id+"F10.wireOp",EDGE,"E76"),sQuery(id+"F10.wireOp",EDGE,"E77"),sQuery(id+"F10.wireOp",EDGE,"E78"),sQuery(id+"F10.wireOp",EDGE,"E79"),sQuery(id+"F10.wireOp",EDGE,"E80"),sQuery(id+"F10.wireOp",EDGE,"E81")])],"isStart":false})});
            var Q1;
            Q1=makeQuery(id+"F11.boolean.opBoolean","COPY",FACE,{"derivedFrom":makeQuery(id+"F11.opExtrude","CAP_FACE",FACE,{"disambiguationData":[OSD([sQuery(id+"F10.wireOp",EDGE,"E82"),sQuery(id+"F10.wireOp",EDGE,"E83"),sQuery(id+"F10.wireOp",EDGE,"E84"),sQuery(id+"F10.wireOp",EDGE,"E85"),sQuery(id+"F10.wireOp",EDGE,"E86"),sQuery(id+"F10.wireOp",EDGE,"E87"),sQuery(id+"F10.wireOp",EDGE,"E88"),sQuery(id+"F10.wireOp",EDGE,"E89"),sQuery(id+"F10.wireOp",EDGE,"E90"),sQuery(id+"F10.wireOp",EDGE,"E91"),sQuery(id+"F10.wireOp",EDGE,"E92"),sQuery(id+"F10.wireOp",EDGE,"E93"),sQuery(id+"F10.wireOp",EDGE,"E94"),sQuery(id+"F10.wireOp",EDGE,"E95")])],"isStart":false})});
            extrude(context, id + "F25", {"entities" : qUnion([Q0, Q1]), "operationType" : NewBodyOperationType.ADD, "depth" : 0.5 * mm, "offsetDistance" : 25 * mm});
        }
        {
            var Q0;
            Q0=makeQuery(id+"F9.boolean.opBoolean","COPY",FACE,{"derivedFrom":makeQuery(id+"F9.opExtrude","CAP_FACE",FACE,{"disambiguationData":[OSD([sQuery(id+"F8.wireOp",EDGE,"E20"),sQuery(id+"F8.wireOp",EDGE,"E21"),sQuery(id+"F8.wireOp",EDGE,"E22"),sQuery(id+"F8.wireOp",EDGE,"E23"),sQuery(id+"F8.wireOp",EDGE,"E24"),sQuery(id+"F8.wireOp",EDGE,"E25"),sQuery(id+"F8.wireOp",EDGE,"E26"),sQuery(id+"F8.wireOp",EDGE,"E27"),sQuery(id+"F8.wireOp",EDGE,"E28"),sQuery(id+"F8.wireOp",EDGE,"E29"),sQuery(id+"F8.wireOp",EDGE,"E30"),sQuery(id+"F8.wireOp",EDGE,"E31"),sQuery(id+"F8.wireOp",EDGE,"E32"),sQuery(id+"F8.wireOp",EDGE,"E33")])],"isStart":false})});
            var Q1;
            Q1=makeQuery(id+"F9.boolean.opBoolean","COPY",FACE,{"derivedFrom":makeQuery(id+"F9.opExtrude","CAP_FACE",FACE,{"disambiguationData":[OSD([sQuery(id+"F8.wireOp",EDGE,"E34"),sQuery(id+"F8.wireOp",EDGE,"E35"),sQuery(id+"F8.wireOp",EDGE,"E36"),sQuery(id+"F8.wireOp",EDGE,"E37")])],"isStart":false})});
            var Q2;
            Q2=makeQuery(id+"F9.boolean.opBoolean","COPY",FACE,{"derivedFrom":makeQuery(id+"F9.opExtrude","CAP_FACE",FACE,{"disambiguationData":[OSD([sQuery(id+"F8.wireOp",EDGE,"E38"),sQuery(id+"F8.wireOp",EDGE,"E39"),sQuery(id+"F8.wireOp",EDGE,"E40"),sQuery(id+"F8.wireOp",EDGE,"E41"),sQuery(id+"F8.wireOp",EDGE,"E42"),sQuery(id+"F8.wireOp",EDGE,"E43"),sQuery(id+"F8.wireOp",EDGE,"E44"),sQuery(id+"F8.wireOp",EDGE,"E45"),sQuery(id+"F8.wireOp",EDGE,"E46"),sQuery(id+"F8.wireOp",EDGE,"E47"),sQuery(id+"F8.wireOp",EDGE,"E48"),sQuery(id+"F8.wireOp",EDGE,"E49"),sQuery(id+"F8.wireOp",EDGE,"E50"),sQuery(id+"F8.wireOp",EDGE,"E51")])],"isStart":false})});
            var Q3;
            Q3=makeQuery(id+"F9.boolean.opBoolean","COPY",FACE,{"derivedFrom":makeQuery(id+"F9.opExtrude","CAP_FACE",FACE,{"disambiguationData":[OSD([sQuery(id+"F8.wireOp",EDGE,"E52"),sQuery(id+"F8.wireOp",EDGE,"E53"),sQuery(id+"F8.wireOp",EDGE,"E54"),sQuery(id+"F8.wireOp",EDGE,"E55"),sQuery(id+"F8.wireOp",EDGE,"E56"),sQuery(id+"F8.wireOp",EDGE,"E57"),sQuery(id+"F8.wireOp",EDGE,"E58"),sQuery(id+"F8.wireOp",EDGE,"E59"),sQuery(id+"F8.wireOp",EDGE,"E60"),sQuery(id+"F8.wireOp",EDGE,"E61"),sQuery(id+"F8.wireOp",EDGE,"E62"),sQuery(id+"F8.wireOp",EDGE,"E63"),sQuery(id+"F8.wireOp",EDGE,"E64"),sQuery(id+"F8.wireOp",EDGE,"E65")])],"isStart":false})});
            extrude(context, id + "F26", {"entities" : qUnion([Q0, Q1, Q2, Q3]), "operationType" : NewBodyOperationType.ADD, "depth" : 0.5 * mm, "offsetDistance" : 25 * mm});
        }
        {
            var Q0;
            Q0=makeQuery(id+"F17.boolean.opBoolean","COPY",FACE,{"derivedFrom":makeQuery(id+"F17.opExtrude","CAP_FACE",FACE,{"disambiguationData":[OSD([sQuery(id+"F16.wireOp",EDGE,"E162"),sQuery(id+"F16.wireOp",EDGE,"E163"),sQuery(id+"F16.wireOp",EDGE,"E164"),sQuery(id+"F16.wireOp",EDGE,"E165"),sQuery(id+"F16.wireOp",EDGE,"E166"),sQuery(id+"F16.wireOp",EDGE,"E167"),sQuery(id+"F16.wireOp",EDGE,"E168"),sQuery(id+"F16.wireOp",EDGE,"E169"),sQuery(id+"F16.wireOp",EDGE,"E170"),sQuery(id+"F16.wireOp",EDGE,"E171"),sQuery(id+"F16.wireOp",EDGE,"E172"),sQuery(id+"F16.wireOp",EDGE,"E173"),sQuery(id+"F16.wireOp",EDGE,"E174"),sQuery(id+"F16.wireOp",EDGE,"E175")])],"isStart":false})});
            var Q1;
            Q1=makeQuery(id+"F17.boolean.opBoolean","COPY",FACE,{"derivedFrom":makeQuery(id+"F17.opExtrude","CAP_FACE",FACE,{"disambiguationData":[OSD([sQuery(id+"F16.wireOp",EDGE,"E176"),sQuery(id+"F16.wireOp",EDGE,"E177"),sQuery(id+"F16.wireOp",EDGE,"E178"),sQuery(id+"F16.wireOp",EDGE,"E179")])],"isStart":false})});
            extrude(context, id + "F27", {"entities" : qUnion([Q0, Q1]), "operationType" : NewBodyOperationType.ADD, "depth" : 0.5 * mm, "offsetDistance" : 25 * mm});
        }
        {
            var Q0;
            Q0=makeQuery(id+"F19.boolean.opBoolean","COPY",FACE,{"derivedFrom":makeQuery(id+"F19.opExtrude","CAP_FACE",FACE,{"disambiguationData":[OSD([sQuery(id+"F18.wireOp",EDGE,"E180"),sQuery(id+"F18.wireOp",EDGE,"E181"),sQuery(id+"F18.wireOp",EDGE,"E182"),sQuery(id+"F18.wireOp",EDGE,"E183"),sQuery(id+"F18.wireOp",EDGE,"E184"),sQuery(id+"F18.wireOp",EDGE,"E185"),sQuery(id+"F18.wireOp",EDGE,"E186"),sQuery(id+"F18.wireOp",EDGE,"E187"),sQuery(id+"F18.wireOp",EDGE,"E188"),sQuery(id+"F18.wireOp",EDGE,"E189"),sQuery(id+"F18.wireOp",EDGE,"E190"),sQuery(id+"F18.wireOp",EDGE,"E191"),sQuery(id+"F18.wireOp",EDGE,"E192"),sQuery(id+"F18.wireOp",EDGE,"E193")])],"isStart":false})});
            var Q1;
            Q1=makeQuery(id+"F19.boolean.opBoolean","COPY",FACE,{"derivedFrom":makeQuery(id+"F19.opExtrude","CAP_FACE",FACE,{"disambiguationData":[OSD([sQuery(id+"F18.wireOp",EDGE,"E194"),sQuery(id+"F18.wireOp",EDGE,"E195"),sQuery(id+"F18.wireOp",EDGE,"E196"),sQuery(id+"F18.wireOp",EDGE,"E197"),sQuery(id+"F18.wireOp",EDGE,"E198"),sQuery(id+"F18.wireOp",EDGE,"E199"),sQuery(id+"F18.wireOp",EDGE,"E200"),sQuery(id+"F18.wireOp",EDGE,"E201"),sQuery(id+"F18.wireOp",EDGE,"E202"),sQuery(id+"F18.wireOp",EDGE,"E203"),sQuery(id+"F18.wireOp",EDGE,"E204"),sQuery(id+"F18.wireOp",EDGE,"E205"),sQuery(id+"F18.wireOp",EDGE,"E206"),sQuery(id+"F18.wireOp",EDGE,"E207")])],"isStart":false})});
            extrude(context, id + "F28", {"entities" : qUnion([Q0, Q1]), "operationType" : NewBodyOperationType.ADD, "depth" : 0.5 * mm, "offsetDistance" : 25 * mm});
        }
    });
